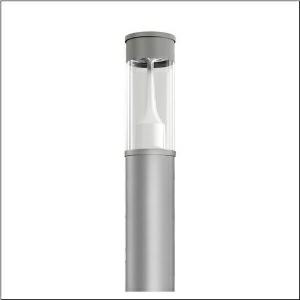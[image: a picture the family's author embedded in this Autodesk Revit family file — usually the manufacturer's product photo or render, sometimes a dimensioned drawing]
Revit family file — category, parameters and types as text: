
# Revit family: city-light_400_iq___p1_0a_5xa5305nf14hp_4342
name_source: partatom
category: Lighting Fixtures
units: mm (PartAtom-declared; Revit-internal decimal feet)

## family parameters
Cut with Voids When Loaded = No
Host = Face
Light Source = No
Part Type = Normal
Room Calculation Point = No
Round Connector Dimension = Use Diameter
Shared = No

## types (1)
- --- (1 x LED, 4210 lm, 33.6 W, 2700K)
    Apparent Load = 34 VA
    CIE Flux Codes = 31 62 91 95 100
    Color Rendering = 70
    Color Temperature = 2700K
    Default Elevation = 1800 mm
    Description = City-Light 400 iQ, light pillar, Module 540 iQ-SR, primary light control with 3 zone facetted reflector, of plastic, silver coated, highly specular, structured, primary optical cover: cover, of PMMA, transparent, partly coated, light distribution: P1.0a, primary light characteristic: strongly asymmetric, LED, High Power LED, rated luminous flux: 4.210lm, luminous efficacy: 125lm/W, light colour: 727, colour temperature: 2700K, control gear: iQ Street-Remote, control: pre-setting: logarithmic dimming characteristic, Street-Remote, Auto-Match, Temp-Guard, Lumen-Switch, Night-Set, Smart-Wire, Light-Fading, Desk-Remote (wireless, voltage-free reading and setting of iQ features in the workshop via application-optimized NFC function/RFID function), optimised constant luminous flux control (CLO 2.0), with terminal, 6-pole, max. 2.5mm², mains connection: 230..240V, AC, 50/60Hz, start of lifetime: 34W, end of service life: 36W, reduction: 15W, luminaire housing, cylindrical, of extruded aluminium section, coated, Siteco® metallic grey (DB 702S), length: 4.694mm, diameter: 200mm, Module 540 iQ-SR, traffic white (RAL 9016), equipment: Power, protection rating (complete): IP65, insulation class (complete): insulation class II (safety insulation), certification: CE, ENEC, VDE, packaging unit: 1 piece

Light Distribution: P1.0a
    Height = 500 mm
    Lamp = 1 x LED
    Lamp Light Flux = 4210 lm
    Lamp Power = 33.6 W
    Lamp count = 1
    Length = 200 mm  [stored 0.656168 ft]
    Luminous efficacy = 125 lm/W
    Manufacturer = Siteco
    ModVariant = No
    Model = 5XA5305NF14HP
    Mounting Place = Floor
    Mounting Type = Freestanding
    Number of Poles = 1
    OnlyDefault = Yes
    Power Factor = 1
    Product Name = City-Light 400 iQ | P1.0a
    Product group = light pillar
    ProductGroupID = 1301
    Protection Class = Protection class II
    Protection Degree = IP 65
    RLX_Detail_Level = 1
    RLX_Emergency_Light_Flux = 0 lm
    RLX_Emergency_Type = 0
    RLX_Emergency_Type_DB = No
    RlxData = <blob elided: 53393 chars, md5=4ba73379>
    Socket = socket
    Standby Power = 0 W
    System Light Flux = 4210 lm
    System Power = 34 W
    Type Comments = factory setting: luminous flux: 100 % | dim-lin: 254 | 695 mA
    Type Image = l_1006916.jpg
    URL = http://relux.com
    VarID = @adj_151957
    Voltage = 0 V
    Weight = 0.00 kg
    Width = 0 mm  [stored 0 ft]

note: [stored X ft] marks values corroborated as IEEE doubles in the binary element streams (Revit-internal decimal feet)

## geometry (parser evidence)
native form markers: Blend x4, Sweep x11
no freeform markers — native parametric forms only
